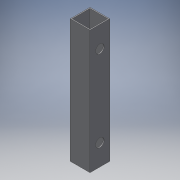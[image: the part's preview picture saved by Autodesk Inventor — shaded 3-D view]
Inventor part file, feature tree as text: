
AUTODESK INVENTOR PART (.ipt)
format: ipt  version: 2018 (Build 220112000, 112)  size: 113,664 bytes
history: native  units: mm
features: other x2, sketch x2, extrude x1, hole x1
ambient origin geometry x8: Origin, YZ Plane, XZ Plane, XY Plane, X Axis, Y Axis, Z Axis, Center Point
bodies: Body1 (feature_tree)
feature tree (6):
  other  "ソリッド1"
  extrude  "押し出し1"  Depth=32.0mm
  other  "作業平面1"
  hole  "穴2"  [1 undecoded]
  sketch  "スケッチ1"
  sketch  "スケッチ6"
note: 1 required parameter value undecoded (feature->parameter linkage not recoverable at this tier; creation-order binding heuristic only, values carry confidence <= 0.55)
